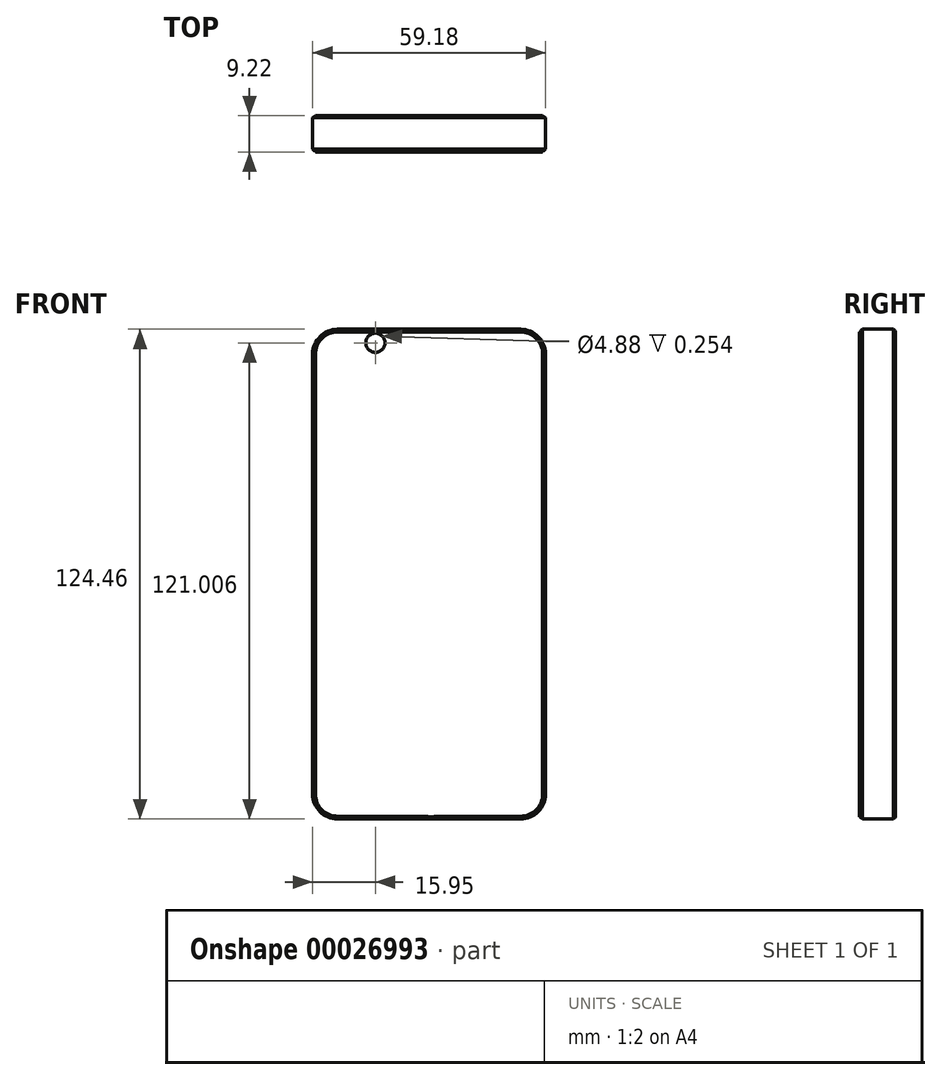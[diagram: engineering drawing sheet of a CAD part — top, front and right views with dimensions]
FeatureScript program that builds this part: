
annotation { "Feature Type Name" : "Feature", "Feature Type Description" : "" }
export const myFeature = defineFeature(function(context is Context, id is Id, definition is map)
    precondition{}
    {
        {
            var Q0;
            Q0=qCreatedBy(makeId("Front.planeOp"),FACE);
            var sketch = newSketch(context, id + "F0", { "sketchPlane" : qUnion([Q0])});
            skLineSegment(sketch, "E0.bottom", {"start": v(-32.64, 54.51) * mm, "end": v(26.54, 54.51) * mm});
            skLineSegment(sketch, "E0.top", {"start": v(-32.64, -69.95) * mm, "end": v(26.54, -69.95) * mm});
            skLineSegment(sketch, "E0.left", {"start": v(-32.64, 54.51) * mm, "end": v(-32.64, -69.95) * mm});
            skLineSegment(sketch, "E0.right", {"start": v(26.54, 54.51) * mm, "end": v(26.54, -69.95) * mm});
            skSolve(sketch);
        }
        {
            var Q0;
            Q0 = qSketchRegion(id + "F0", true);
            extrude(context, id + "F1", {"entities" : qUnion([Q0]), "depth" : 8.97 * mm});
        }
        {
            var Q0;
            Q0=makeQuery(id+"F1.opExtrude","SWEPT_EDGE",EDGE,{"disambiguationData":[OSD([sQuery(id+"F0.wireOp",EDGE,"E0.bottom"),sQuery(id+"F0.wireOp",EDGE,"E0.right")])]});
            var Q1;
            Q1=makeQuery(id+"F1.opExtrude","SWEPT_EDGE",EDGE,{"disambiguationData":[OSD([sQuery(id+"F0.wireOp",EDGE,"E0.bottom"),sQuery(id+"F0.wireOp",EDGE,"E0.left")])]});
            var Q2;
            Q2=makeQuery(id+"F1.opExtrude","SWEPT_EDGE",EDGE,{"disambiguationData":[OSD([sQuery(id+"F0.wireOp",EDGE,"E0.top"),sQuery(id+"F0.wireOp",EDGE,"E0.right")])]});
            var Q3;
            Q3=makeQuery(id+"F1.opExtrude","SWEPT_EDGE",EDGE,{"disambiguationData":[OSD([sQuery(id+"F0.wireOp",EDGE,"E0.top"),sQuery(id+"F0.wireOp",EDGE,"E0.left")])]});
            fillet(context, id + "F2", {"entities" : qUnion([Q0, Q1, Q2, Q3]), "radius" : 6.35 * mm, "tangentPropagation" : true, "allowEdgeOverflow" : false});
        }
        {
            var Q0;
            Q0=makeQuery(id+"F1.opExtrude","CAP_EDGE",EDGE,{"disambiguationData":[OSD([sQuery(id+"F0.wireOp",EDGE,"E0.right")])],"isStart":false});
            var Q1;
            Q1=makeQuery(id+"F1.opExtrude","CAP_EDGE",EDGE,{"disambiguationData":[OSD([sQuery(id+"F0.wireOp",EDGE,"E0.right")])],"isStart":true});
            chamfer(context, id + "F3", {"entities" : qUnion([Q0, Q1]), "width" : 0.5 * mm, "tangentPropagation" : true});
        }
        {
            var Q0;
            Q0=makeQuery(id+"F1.opExtrude","CAP_FACE",FACE,{"disambiguationData":[OSD([sQuery(id+"F0.wireOp",EDGE,"E0.bottom"),sQuery(id+"F0.wireOp",EDGE,"E0.top"),sQuery(id+"F0.wireOp",EDGE,"E0.left"),sQuery(id+"F0.wireOp",EDGE,"E0.right")])],"isStart":true});
            chamfer(context, id + "F4", {"entities" : qUnion([Q0]), "width" : 0.5 * mm, "tangentPropagation" : true});
        }
        {
            var Q0;
            Q0=makeQuery(id+"F1.opExtrude","CAP_FACE",FACE,{"disambiguationData":[OSD([sQuery(id+"F0.wireOp",EDGE,"E0.bottom"),sQuery(id+"F0.wireOp",EDGE,"E0.top"),sQuery(id+"F0.wireOp",EDGE,"E0.left"),sQuery(id+"F0.wireOp",EDGE,"E0.right")])],"isStart":false});
            chamfer(context, id + "F5", {"entities" : qUnion([Q0]), "width" : 0.5 * mm, "tangentPropagation" : true});
        }
        {
            var Q0;
            Q0=makeQuery(id+"F1.opExtrude","CAP_FACE",FACE,{"disambiguationData":[OSD([sQuery(id+"F0.wireOp",EDGE,"E0.bottom"),sQuery(id+"F0.wireOp",EDGE,"E0.top"),sQuery(id+"F0.wireOp",EDGE,"E0.left"),sQuery(id+"F0.wireOp",EDGE,"E0.right")])],"isStart":false});
            var sketch = newSketch(context, id + "F6", { "sketchPlane" : qUnion([Q0])});
            skLineSegment(sketch, "E1.bottom", {"start": v(-31.63, 48.16) * mm, "end": v(25.52, 48.16) * mm});
            skLineSegment(sketch, "E1.top", {"start": v(-31.63, -63.6) * mm, "end": v(25.52, -63.6) * mm});
            skLineSegment(sketch, "E1.left", {"start": v(-31.63, 48.16) * mm, "end": v(-31.63, -63.6) * mm});
            skLineSegment(sketch, "E1.right", {"start": v(25.52, 48.16) * mm, "end": v(25.52, -63.6) * mm});
            skSolve(sketch);
        }
        {
            var Q0;
            Q0 = qSketchRegion(id + "F6", true);
            extrude(context, id + "F7", {"entities" : qUnion([Q0]), "depth" : 0.03 * mm});
        }
        {
            var Q0;
            Q0=makeQuery(id+"F1.opExtrude","CAP_FACE",FACE,{"disambiguationData":[OSD([sQuery(id+"F0.wireOp",EDGE,"E0.bottom"),sQuery(id+"F0.wireOp",EDGE,"E0.top"),sQuery(id+"F0.wireOp",EDGE,"E0.left"),sQuery(id+"F0.wireOp",EDGE,"E0.right")])],"isStart":false});
            var sketch = newSketch(context, id + "F8", { "sketchPlane" : qUnion([Q0])});
            skCircle(sketch, "E2", {"center": v(-16.7, 51.06) * mm, "radius": 2.44 * mm});
            skSolve(sketch);
        }
        {
            var Q0;
            Q0=makeQuery(id+"F1.opExtrude","SWEPT_FACE",FACE,{"disambiguationData":[OSD([sQuery(id+"F0.wireOp",EDGE,"E0.bottom")])]});
            var sketch = newSketch(context, id + "F9", { "sketchPlane" : qUnion([Q0])});
            skEllipse(sketch, "E3", {"center": v(12.45, -4.6) * mm, "majorRadius": 6.47 * mm, "minorRadius": 3.05 * mm, "majorAxis": v(-1, 0)});
            skSolve(sketch);
        }
        {
            var Q0;
            Q0=sQuery(id+"F9.wireOp",EDGE,"E3");
            extrude(context, id + "F10", {"bodyType" : ToolBodyType.SURFACE, "operationType" : NewBodyOperationType.ADD, "surfaceEntities" : qUnion([Q0]), "depth" : 1.02 * mm});
        }
        {
            var Q0;
            {var subQ8=sQuery(id+"F8.wireOp",EDGE,"E2");Q0=makeQuery(id+"F8.imprint","IMPRINT",FACE,{"disambiguationData":[TD([[makeQuery(id+"F8.imprint","IMPRINT",EDGE,{"derivedFrom":subQ8}),-1.0]])]});}
            var sketch = newSketch(context, id + "F11", { "sketchPlane" : qUnion([Q0])});
            skCircle(sketch, "E4", {"center": v(-2.59, -66.3) * mm, "radius": 3.1 * mm});
            skSolve(sketch);
        }
        {
            var Q0;
            Q0 = qSketchRegion(id + "F11", true);
            var Q1;
            {var subQ8=sQuery(id+"F8.wireOp",EDGE,"E2");Q1=makeQuery(id+"F8.imprint","IMPRINT",FACE,{"disambiguationData":[TD([[makeQuery(id+"F8.imprint","IMPRINT",EDGE,{"derivedFrom":subQ8}),-1.0]])]});}
            extrude(context, id + "F12", {"entities" : qUnion([Q0, Q1]), "operationType" : NewBodyOperationType.ADD, "depth" : 0.25 * mm});
        }
    });
